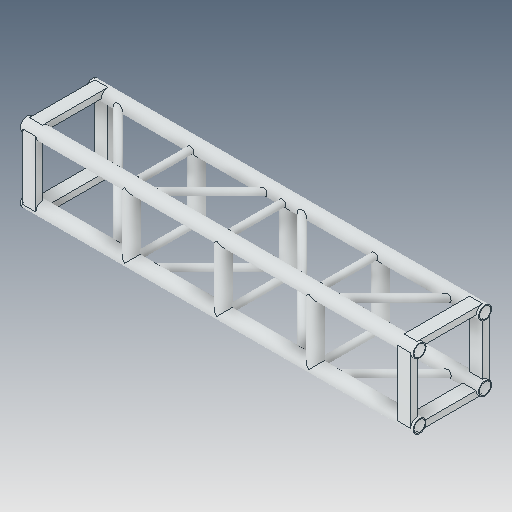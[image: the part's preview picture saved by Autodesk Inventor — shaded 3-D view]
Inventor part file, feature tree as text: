
AUTODESK INVENTOR PART (.ipt)
format: ipt  version: 2023.5 (Build 275446000, 446)  size: 332,288 bytes
history: native  units: in
note: dims shown in document units (in); Inventor stores cm internally (conversion verified against a paired STEP export)
features: imported_body x27, other x3, mirror x3
ambient origin geometry x8: Origin, YZ Plane, XZ Plane, XY Plane, X Axis, Y Axis, Z Axis, Center Point
bodies: Solid1 (feature_tree), Solid2 (feature_tree), Solid3 (feature_tree), Solid4 (feature_tree), Solid5 (feature_tree), Solid6 (feature_tree), Solid7 (feature_tree), Solid8 (feature_tree), Solid9 (feature_tree), Solid10 (feature_tree), Solid11 (feature_tree), Solid12 (feature_tree), Solid13 (feature_tree), Solid14 (feature_tree), Solid15 (feature_tree), Solid16 (feature_tree), Solid17 (feature_tree), Solid18 (feature_tree), Solid19 (feature_tree), Solid20 (feature_tree), Solid21 (feature_tree), Solid22 (feature_tree), Solid23 (feature_tree), Solid24 (feature_tree), Solid25 (feature_tree), Solid26 (feature_tree), Solid27 (feature_tree), Solid28 (feature_tree), Solid29 (feature_tree), Solid30 (feature_tree), Solid31 (feature_tree), Solid32 (feature_tree), Solid33 (feature_tree)
feature tree (33):
  imported_body  "Imported1"
  imported_body  "Imported2"
  imported_body  "Imported3"
  imported_body  "Imported4"
  imported_body  "Imported5"
  imported_body  "Imported6"
  imported_body  "Imported7"
  imported_body  "Imported8"
  imported_body  "Imported9"
  imported_body  "Imported10"
  imported_body  "Imported11"
  imported_body  "Imported12"
  imported_body  "Imported13"
  imported_body  "Imported14"
  imported_body  "Imported15"
  imported_body  "Imported16"
  imported_body  "Imported17"
  imported_body  "Imported18"
  imported_body  "Imported19"
  imported_body  "Imported20"
  imported_body  "Imported21"
  imported_body  "Imported22"
  imported_body  "Imported23"
  imported_body  "Imported24"
  imported_body  "Imported25"
  imported_body  "Imported26"
  imported_body  "Imported27"
  other  "Cut-Extrude1[1]"
  other  "Cut-Extrude1[2]"
  other  "Cut-Extrude1[3]"
  mirror  "Mirror1[1]"
  mirror  "Mirror1[2]"
  mirror  "Mirror1[3]"
